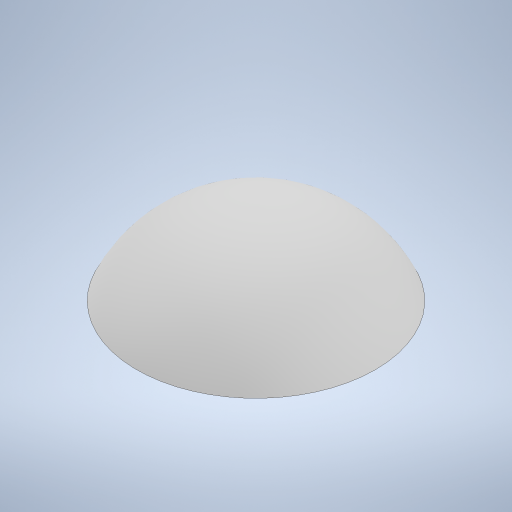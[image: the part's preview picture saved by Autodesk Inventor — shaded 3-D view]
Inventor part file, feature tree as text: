
AUTODESK INVENTOR PART (.ipt)
format: ipt  version: 2024.2 (Build 282272000, 272)  size: 225,792 bytes
history: native  units: in
note: dims shown in document units (in); Inventor stores cm internally (conversion verified against a paired STEP export)
features: revolve x1, sketch x1
ambient origin geometry x8: Origin, YZ Plane, XZ Plane, XY Plane, X Axis, Y Axis, Z Axis, Center Point
bodies: Solid1 (feature_tree)
feature tree (2):
  revolve  "Revolution1"  Angle=90.0deg
  sketch  "Sketch1"  dims[d0=0.675in d1=90.0deg]
